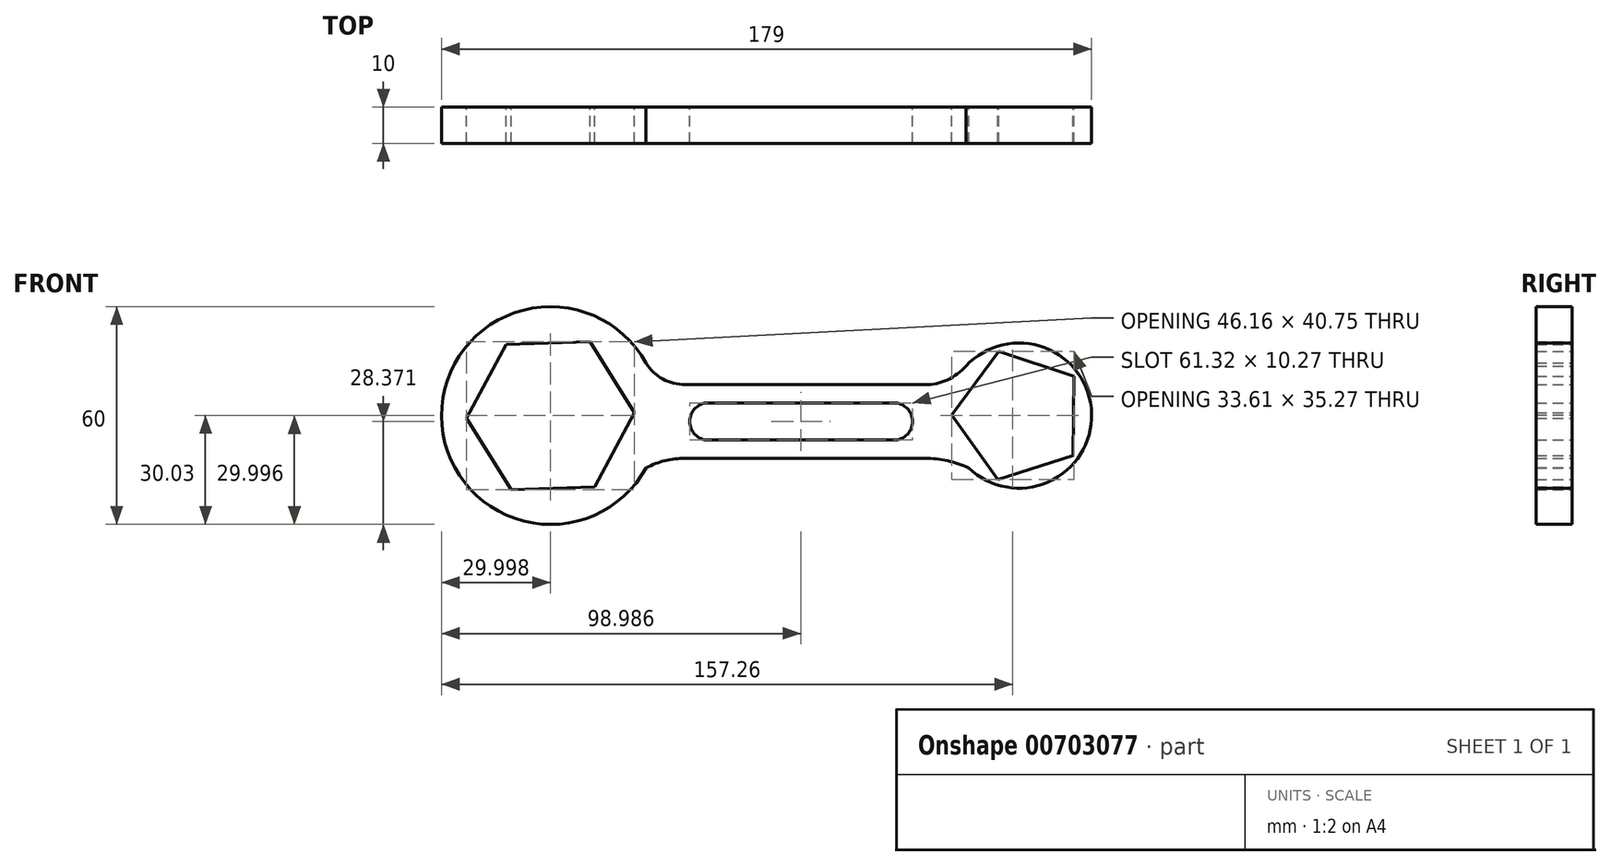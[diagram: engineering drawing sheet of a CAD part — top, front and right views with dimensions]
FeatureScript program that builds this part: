
annotation { "Feature Type Name" : "Feature", "Feature Type Description" : "" }
export const myFeature = defineFeature(function(context is Context, id is Id, definition is map)
    precondition{}
    {
        {
            var Q0;
            Q0=qCreatedBy(makeId("Front.planeOp"),FACE);
            var sketch = newSketch(context, id + "F0", { "sketchPlane" : qUnion([Q0])});
            skCircle(sketch, "E0", {"center": v(-45.15, 8.67) * mm, "radius": 30 * mm});
            skCircle(sketch, "E1.cCircle", {"center": v(-45.15, 8.67) * mm, "radius": 20 * mm, "construction": true});
            skLineSegment(sketch, "E1.0", {"start": v(-34.28, 29.04) * mm, "end": v(-22.07, 9.44) * mm});
            skLineSegment(sketch, "E1.1", {"start": v(-22.07, 9.44) * mm, "end": v(-32.94, -10.93) * mm});
            skLineSegment(sketch, "E1.2", {"start": v(-32.94, -10.93) * mm, "end": v(-56.02, -11.71) * mm});
            skLineSegment(sketch, "E1.3", {"start": v(-56.02, -11.71) * mm, "end": v(-68.23, 7.89) * mm});
            skLineSegment(sketch, "E1.4", {"start": v(-68.23, 7.89) * mm, "end": v(-57.36, 28.27) * mm});
            skLineSegment(sketch, "E1.5", {"start": v(-57.36, 28.27) * mm, "end": v(-34.28, 29.04) * mm});
            skPoint(sketch, "E1.0.midPoint", {"position": v(-28.18, 19.24) * mm});
            skPoint(sketch, "E2.center.orphan", {"position": v(83.85, 8.67) * mm});
            skPoint(sketch, "E3.start.orphan", {"position": v(70.14, -5.83) * mm});
            skCircle(sketch, "E4", {"center": v(83.85, 8.67) * mm, "radius": 20 * mm});
            skPoint(sketch, "E5.start.orphan", {"position": v(57.99, 15.34) * mm});
            skPoint(sketch, "E6.end.orphan", {"position": v(57.99, -5.83) * mm});
            skLineSegment(sketch, "E7", {"start": v(-8.04, 17.17) * mm, "end": v(57.99, 17.17) * mm});
            skLineSegment(sketch, "E8", {"start": v(57.99, 17.17) * mm, "end": v(57.99, 15.34) * mm});
            skLineSegment(sketch, "E9", {"start": v(57.99, -3.1) * mm, "end": v(-8.04, -3.1) * mm});
            skArc(sketch, "E10", {"start": v(-18.86, 23.12) * mm, "mid": v(-14.21, 18.76) * mm, "end": v(-8.04, 17.17) * mm});
            skArc(sketch, "E11", {"start": v(-8.04, -3.1) * mm, "mid": v(-13.58, -3.75) * mm, "end": v(-18.8, -5.69) * mm});
            skArc(sketch, "E12", {"start": v(57.99, 17.17) * mm, "mid": v(64.17, 18.52) * mm, "end": v(69.24, 22.32) * mm});
            skArc(sketch, "E13", {"start": v(70.14, -5.83) * mm, "mid": v(64.22, -3.79) * mm, "end": v(57.99, -3.1) * mm});
            skPoint(sketch, "E14.0.midPoint", {"position": v(97.38, 15.14) * mm});
            skPoint(sketch, "E15.orphan", {"position": v(93.64, 22.95) * mm});
            skPoint(sketch, "E16.orphan", {"position": v(101.12, 7.33) * mm});
            skPoint(sketch, "E17.orphan", {"position": v(74.06, -5.62) * mm});
            skPoint(sketch, "E14.4.start.orphan", {"position": v(66.58, 11.09) * mm});
            skCircle(sketch, "E18.cCircle", {"center": v(83.85, 8.67) * mm, "radius": 15 * mm, "construction": true});
            skLineSegment(sketch, "E18.0", {"start": v(78.22, 26.33) * mm, "end": v(98.91, 19.47) * mm});
            skLineSegment(sketch, "E18.1", {"start": v(98.91, 19.47) * mm, "end": v(98.78, -2.32) * mm});
            skLineSegment(sketch, "E18.2", {"start": v(98.78, -2.32) * mm, "end": v(78.01, -8.93) * mm});
            skLineSegment(sketch, "E18.3", {"start": v(78.01, -8.93) * mm, "end": v(65.3, 8.78) * mm});
            skLineSegment(sketch, "E18.4", {"start": v(65.3, 8.78) * mm, "end": v(78.22, 26.33) * mm});
            skPoint(sketch, "E18.0.midPoint", {"position": v(88.57, 22.9) * mm});
            skPoint(sketch, "E19.start.orphan", {"position": v(49.36, 11.09) * mm});
            skPoint(sketch, "E20.start.orphan", {"position": v(49.36, 0) * mm});
            skPoint(sketch, "E21.end.orphan", {"position": v(0, 10) * mm});
            skLineSegment(sketch, "E22", {"start": v(-1.7, 12.17) * mm, "end": v(49.36, 12.17) * mm});
            skLineSegment(sketch, "E23", {"start": v(-1.7, 1.9) * mm, "end": v(49.36, 1.9) * mm});
            skLineSegment(sketch, "E24", {"start": v(49.36, 11.09) * mm, "end": v(49.36, 12.17) * mm});
            skArc(sketch, "E25", {"start": v(-1.7, 12.17) * mm, "mid": v(-6.82, 7.04) * mm, "end": v(-1.7, 1.9) * mm});
            skArc(sketch, "E26", {"start": v(49.36, 1.9) * mm, "mid": v(54.5, 7.04) * mm, "end": v(49.36, 12.17) * mm});
            skSolve(sketch);
        }
        {
            var Q0;
            Q0=makeQuery(id+"F0.imprint","IMPRINT",FACE,{"disambiguationData":[TD([[makeQuery(id+"F0.imprint","IMPRINT",EDGE,{"derivedFrom":sQuery(id+"F0.wireOp",EDGE,"E1.0")}),1.0]])]});
            var Q1;
            {var subQ5=sQuery(id+"F0.wireOp",EDGE,"E7");Q1=makeQuery(id+"F0.imprint","IMPRINT",FACE,{"disambiguationData":[TD([[makeQuery(id+"F0.imprint","IMPRINT",EDGE,{"derivedFrom":subQ5}),-1.0]])]});}
            var Q2;
            Q2=makeQuery(id+"F0.imprint","IMPRINT",FACE,{"disambiguationData":[TD([[makeQuery(id+"F0.imprint","IMPRINT",EDGE,{"derivedFrom":sQuery(id+"F0.wireOp",EDGE,"E18.0")}),1.0]])]});
            extrude(context, id + "F1", {"entities" : qUnion([Q0, Q1, Q2]), "depth" : 10 * mm, "offsetDistance" : 25 * mm});
        }
    });
